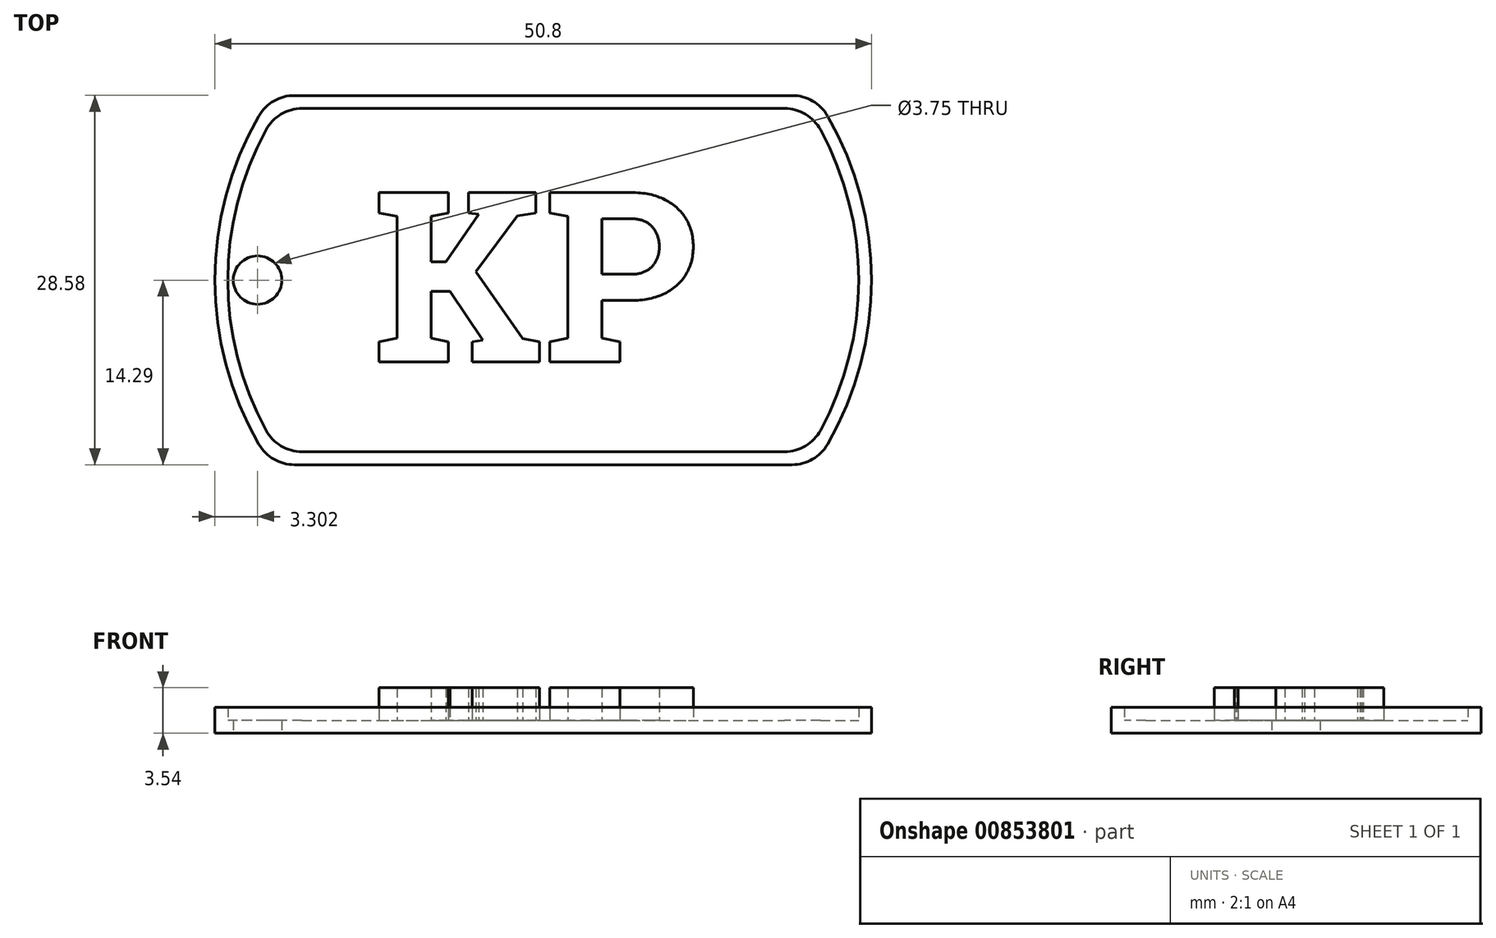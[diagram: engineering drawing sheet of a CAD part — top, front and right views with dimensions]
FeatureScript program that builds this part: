
annotation { "Feature Type Name" : "Feature", "Feature Type Description" : "" }
export const myFeature = defineFeature(function(context is Context, id is Id, definition is map)
    precondition{}
    {
        {
            var Q0;
            Q0=qCreatedBy(makeId("Top.planeOp"),FACE);
            var sketch = newSketch(context, id + "F0", { "sketchPlane" : qUnion([Q0])});
            skArc(sketch, "E0", {"start": v(-22, 12.7) * mm, "mid": v(-25.4, 0) * mm, "end": v(-22, -12.7) * mm});
            skLineSegment(sketch, "E1.top", {"start": v(-19.25, -14.29) * mm, "end": v(19.25, -14.29) * mm});
            skArc(sketch, "E2.trimOffspring", {"start": v(22, -12.7) * mm, "mid": v(25.4, 0) * mm, "end": v(22, 12.7) * mm});
            skLineSegment(sketch, "E3", {"start": v(-19.25, 14.29) * mm, "end": v(19.25, 14.29) * mm});
            skPoint(sketch, "E4.visualSharp", {"position": v(-21, 14.29) * mm});
            skArc(sketch, "E4.filletArc", {"start": v(-19.25, 14.29) * mm, "mid": v(-20.83, 13.86) * mm, "end": v(-22, 12.7) * mm});
            skPoint(sketch, "E5.visualSharp", {"position": v(21, 14.29) * mm});
            skArc(sketch, "E5.filletArc", {"start": v(22, 12.7) * mm, "mid": v(20.83, 13.86) * mm, "end": v(19.25, 14.29) * mm});
            skPoint(sketch, "E6.visualSharp", {"position": v(21, -14.29) * mm});
            skArc(sketch, "E6.filletArc", {"start": v(19.25, -14.29) * mm, "mid": v(20.83, -13.86) * mm, "end": v(22, -12.7) * mm});
            skPoint(sketch, "E7.visualSharp", {"position": v(-21, -14.29) * mm});
            skArc(sketch, "E7.filletArc", {"start": v(-22, -12.7) * mm, "mid": v(-20.83, -13.86) * mm, "end": v(-19.25, -14.29) * mm});
            skCircle(sketch, "E8", {"center": v(-22.1, 0) * mm, "radius": 1.87 * mm});
            skSolve(sketch);
        }
        {
            var Q0;
            Q0=makeQuery(id+"F0.imprint","IMPRINT",FACE,{"disambiguationData":[TD([[makeQuery(id+"F0.imprint","IMPRINT",EDGE,{"derivedFrom":sQuery(id+"F0.wireOp",EDGE,"E0")}),1.0]])]});
            extrude(context, id + "F1", {"entities" : qUnion([Q0]), "depth" : 1 * mm, "offsetDistance" : 25.4 * mm});
        }
        {
            var Q0;
            Q0=makeQuery(id+"F1.opExtrude","CAP_FACE",FACE,{"disambiguationData":[OSD([sQuery(id+"F0.wireOp",EDGE,"E0"),sQuery(id+"F0.wireOp",EDGE,"E1.top"),sQuery(id+"F0.wireOp",EDGE,"E2.trimOffspring"),sQuery(id+"F0.wireOp",EDGE,"E3"),sQuery(id+"F0.wireOp",EDGE,"E4.filletArc"),sQuery(id+"F0.wireOp",EDGE,"E5.filletArc"),sQuery(id+"F0.wireOp",EDGE,"E6.filletArc"),sQuery(id+"F0.wireOp",EDGE,"E7.filletArc")])],"isStart":false});
            var sketch = newSketch(context, id + "F2", { "sketchPlane" : qUnion([Q0])});
            skLineSegment(sketch, "E9.0", {"start": v(-18.66, 13.29) * mm, "end": v(18.66, 13.29) * mm});
            skArc(sketch, "E9.1", {"start": v(-21.45, 11.63) * mm, "mid": v(-24.4, 0) * mm, "end": v(-21.45, -11.63) * mm});
            skLineSegment(sketch, "E9.2", {"start": v(-18.66, -13.29) * mm, "end": v(18.66, -13.29) * mm});
            skArc(sketch, "E9.3", {"start": v(21.45, -11.63) * mm, "mid": v(24.4, 0) * mm, "end": v(21.45, 11.63) * mm});
            skPoint(sketch, "E10.visualSharp", {"position": v(-20.46, 13.29) * mm});
            skArc(sketch, "E10.filletArc", {"start": v(-18.66, 13.29) * mm, "mid": v(-20.29, 12.84) * mm, "end": v(-21.45, 11.63) * mm});
            skPoint(sketch, "E11.visualSharp", {"position": v(20.46, 13.29) * mm});
            skArc(sketch, "E11.filletArc", {"start": v(21.45, 11.63) * mm, "mid": v(20.29, 12.84) * mm, "end": v(18.66, 13.29) * mm});
            skPoint(sketch, "E12.visualSharp", {"position": v(20.46, -13.29) * mm});
            skArc(sketch, "E12.filletArc", {"start": v(18.66, -13.29) * mm, "mid": v(20.29, -12.84) * mm, "end": v(21.45, -11.63) * mm});
            skPoint(sketch, "E13.visualSharp", {"position": v(-20.46, -13.29) * mm});
            skArc(sketch, "E13.filletArc", {"start": v(-21.45, -11.63) * mm, "mid": v(-20.29, -12.84) * mm, "end": v(-18.66, -13.29) * mm});
            skLineSegment(sketch, "E14.0", {"start": v(-19.25, 14.29) * mm, "end": v(19.25, 14.29) * mm});
            skArc(sketch, "E14.1", {"start": v(-22, 12.7) * mm, "mid": v(-25.4, 0) * mm, "end": v(-22, -12.7) * mm});
            skLineSegment(sketch, "E14.2", {"start": v(-19.25, -14.29) * mm, "end": v(19.25, -14.29) * mm});
            skArc(sketch, "E14.3", {"start": v(22, -12.7) * mm, "mid": v(25.4, 0) * mm, "end": v(22, 12.7) * mm});
            skPoint(sketch, "E15.visualSharp", {"position": v(-21, -14.29) * mm});
            skArc(sketch, "E15.filletArc", {"start": v(-22, -12.7) * mm, "mid": v(-20.83, -13.86) * mm, "end": v(-19.25, -14.29) * mm});
            skPoint(sketch, "E16.visualSharp", {"position": v(21, -14.29) * mm});
            skArc(sketch, "E16.filletArc", {"start": v(19.25, -14.29) * mm, "mid": v(20.83, -13.86) * mm, "end": v(22, -12.7) * mm});
            skPoint(sketch, "E17.visualSharp", {"position": v(21, 14.29) * mm});
            skArc(sketch, "E17.filletArc", {"start": v(22, 12.7) * mm, "mid": v(20.83, 13.86) * mm, "end": v(19.25, 14.29) * mm});
            skPoint(sketch, "E18.visualSharp", {"position": v(-21, 14.29) * mm});
            skArc(sketch, "E18.filletArc", {"start": v(-19.25, 14.29) * mm, "mid": v(-20.83, 13.86) * mm, "end": v(-22, 12.7) * mm});
            skSolve(sketch);
        }
        {
            var Q0;
            Q0=makeQuery(id+"F2.imprint","IMPRINT",FACE,{"disambiguationData":[TD([[makeQuery(id+"F2.imprint","IMPRINT",EDGE,{"derivedFrom":sQuery(id+"F2.wireOp",EDGE,"E9.0")}),1.0]])]});
            extrude(context, id + "F3", {"entities" : qUnion([Q0]), "operationType" : NewBodyOperationType.ADD, "depth" : 1 * mm, "offsetDistance" : 25.4 * mm});
        }
        {
            var Q0;
            Q0=makeQuery(id+"F1.opExtrude","CAP_FACE",FACE,{"disambiguationData":[OSD([sQuery(id+"F0.wireOp",EDGE,"E0"),sQuery(id+"F0.wireOp",EDGE,"E1.top"),sQuery(id+"F0.wireOp",EDGE,"E2.trimOffspring"),sQuery(id+"F0.wireOp",EDGE,"E3"),sQuery(id+"F0.wireOp",EDGE,"E4.filletArc"),sQuery(id+"F0.wireOp",EDGE,"E5.filletArc"),sQuery(id+"F0.wireOp",EDGE,"E6.filletArc"),sQuery(id+"F0.wireOp",EDGE,"E7.filletArc"),sQuery(id+"F0.wireOp",EDGE,"E8")])],"isStart":false});
            var sketch = newSketch(context, id + "F4", { "sketchPlane" : qUnion([Q0])});
            skText(sketch, "E19", { "text": "KP", "fontName": "RobotoSlab-Bold.ttf"});
            const initialGuessF4  = {"E19": [-0.0132, -0.00634, 1, 0, 0.01329]};
            skSetInitialGuess(sketch, initialGuessF4);
            skSolve(sketch);
        }
        {
            var Q0;
            Q0 = qSketchRegion(id + "F4", true);
            extrude(context, id + "F5", {"entities" : qUnion([Q0]), "operationType" : NewBodyOperationType.ADD, "depth" : 2.54 * mm, "offsetDistance" : 25.4 * mm});
        }
    });
